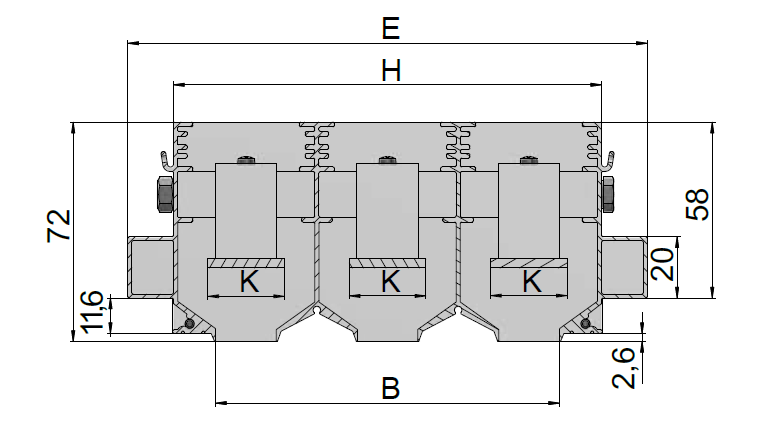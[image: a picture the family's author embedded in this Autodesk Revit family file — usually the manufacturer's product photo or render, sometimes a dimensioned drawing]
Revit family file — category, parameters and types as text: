
# Revit family: GR_Адаптер линейный_Муфта(1)_VL-G-КСД-У_R21
name_source: partatom
category: Соединительные детали воздуховодов
units: mm (PartAtom-declared; Revit-internal decimal feet)

## family parameters
Всегда вертикально = Да
Заголовок OmniClass = Metal Ducts
На основе рабочей плоскости = Нет
Номер OmniClass = 23.75.70.14.31
Общий = Нет
При загрузке вырезать с полостями = Нет
Размер круглого соединителя = Использовать диаметр
Тип детали = Мультипорт

## types (15) — shared parameters
ADSK_URL страницы изделия = https://grilles.ru
ADSK_Версия Revit = 2021
ADSK_Единица измерения = шт.
ADSK_Завод-изготовитель = ООО "ВЕНТРЕШЕТКИКОМ"
ADSK_Код изделия = 000158
ADSK_Количество = 1
ADSK_Материал = ADSK_Оцинкованная сталь
ADSK_Наименование = VL-G-КСД-У, адаптер вентиляционной решётки
Изготовитель = ООО "ВЕНТРЕШЕТКИКОМ"
Корпус_Металл_Толщина = 1 мм
Муфта_Металл_Толщина = 1 мм
zero-valued in all types: Отметка по умолчанию

## per-type parameters (varying)
| type | Корпус_Высота | Корпус_Длина | Муфта_БВ_Отступ_Вер | Муфта_Отступ_Гор | Решетка_отступ | Решётка_Высота |
| VL-G-КСД-У 1-20 | 180 мм | 191 мм | 75 мм | 96 мм | 37 мм | 72 мм |
| VL-G-КСД-У 1-30 | 180 мм | 201 мм | 75 мм | 101 мм | 42 мм | 82 мм |
| VL-G-КСД-У 1-40 | 220 мм | 211 мм | 95 мм | 106 мм | 47 мм | 92 мм |
| VL-G-КСД-У 1-50 | 220 мм | 221 мм | 95 мм | 111 мм | 52 мм | 102 мм |
| VL-G-КСД-У 1-60 | 270 мм | 231 мм | 120 мм | 116 мм | 57 мм | 112 мм |
| VL-G-КСД-У 1-70 | 270 мм | 241 мм | 120 мм | 121 мм | 62 мм | 122 мм |
| VL-G-КСД-У 2-20 | 220 мм | 231 мм | 95 мм | 116 мм | 57 мм | 112 мм |
| VL-G-КСД-У 2-25 | 220 мм | 241 мм | 95 мм | 121 мм | 62 мм | 122 мм |
| VL-G-КСД-У 2-30 | 220 мм | 251 мм | 95 мм | 126 мм | 67 мм | 132 мм |
| VL-G-КСД-У 3-20 | 220 мм | 271 мм | 95 мм | 136 мм | 77 мм | 152 мм |
| VL-G-КСД-У 3-25 | 220 мм | 286 мм | 95 мм | 143 мм | 85 мм | 167 мм |
| VL-G-КСД-У 3-30 | 220 мм | 301 мм | 95 мм | 151 мм | 92 мм | 182 мм |
| VL-G-КСД-У 4-20 | 270 мм | 311 мм | 120 мм | 156 мм | 97 мм | 192 мм |
| VL-G-КСД-У 4-25 | 270 мм | 331 мм | 120 мм | 166 мм | 107 мм | 212 мм |
| VL-G-КСД-У 4-30 | 270 мм | 351 мм | 120 мм | 176 мм | 117 мм | 232 мм |

note: column(s) folded — value = type name in every type: ADSK_Марка
